# Revit family: 31_CC_MOD_Damm_overheaddeur
name_source: partatom
category: Doors
units: mm (PartAtom-declared; Revit-internal decimal feet)

## family parameters
Always vertical = Yes
Cut with Voids When Loaded = No
Host = Wall
OmniClass Number = 23.30.10.00
OmniClass Title = Doors
Room Calculation Point = No
Shared = No

## types (4) — shared parameters
Analytic Construction = <None>
Frame Projection Ext. = 25 mm  [stored 0.082021 ft]
Frame Projection Int. = 25 mm  [stored 0.082021 ft]
Frame Width = 76 mm
Function = Interior
Height = 2134 mm
Rubber = Rubber
Wall Closure = By host
aluminium = Aluminium
breedte_hoeklijn = 135 mm  [stored 0.442913 ft]
dagmaat = 3000 mm  [stored 9.84252 ft]
dagmaathoogte = 3000 mm  [stored 9.84252 ft]
glasoverheaddeur = Glas overheaddeur
lengte_hoeklijn = 5290 mm
rail_dikte = 95 mm
staal = Staal
tussen_stijl = 100 mm  [stored 0.328084 ft]
zijstijl = 65 mm

## per-type parameters (varying)
| type | Half ramen | Manufacturer | Model | URL | Width | breedte_helft_overheaddeur | dagmaatbreedte | half_dicht | maximale_dagmaatbreedte | maximale_dagmaathoogte | minimale_dagmaatbreedte | minimale_dagmaathoogte | panelen dicht | raam_breedte | ramen dicht |
| Overhead deur geheel glas | Yes | Damm deuren | Overheaddeur GDB-60 | www.dammdeuren.nl | 4000 mm  [stored 13.1234 ft] | 2000 mm  [stored 6.56168 ft] | 4000 mm  [stored 13.1234 ft] | No | 5999 mm | 3000 mm  [stored 9.84252 ft] | 1999 mm | 2000 mm  [stored 6.56168 ft] | No | 900 mm  [stored 2.95276 ft] | Yes |
| Overhead deur ramen gehalveerd | No |  |  |  | 4999 mm | 2500 mm | 4999 mm | Yes | 0 mm  [stored 0 ft] | 0 mm  [stored 0 ft] | 0 mm  [stored 0 ft] | 0 mm  [stored 0 ft] | No | 1150 mm | Yes |
| Overhead deur zonder ramen | No |  |  |  | 4999 mm | 2500 mm | 4999 mm | Yes | 0 mm  [stored 0 ft] | 0 mm  [stored 0 ft] | 0 mm  [stored 0 ft] | 0 mm  [stored 0 ft] | Yes | 1150 mm | No |
| Overhead deur geheel glas kl | Yes | Damm deuren | Overheaddeur GDB-60 | www.dammdeuren.nl | 4000 mm  [stored 13.1234 ft] | 2000 mm  [stored 6.56168 ft] | 4000 mm  [stored 13.1234 ft] | No | 5999 mm | 3000 mm  [stored 9.84252 ft] | 1999 mm | 2000 mm  [stored 6.56168 ft] | No | 900 mm  [stored 2.95276 ft] | Yes |

note: [stored X ft] marks values corroborated as IEEE doubles in the binary element streams (Revit-internal decimal feet)

## geometry (parser evidence)
native form markers: Blend x8, Sweep x2
no freeform markers — native parametric forms only
